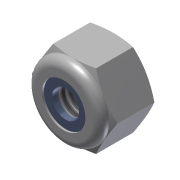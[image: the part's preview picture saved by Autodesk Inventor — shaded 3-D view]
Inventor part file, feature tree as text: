
AUTODESK INVENTOR PART (.ipt)
format: ipt  version: 2013 (Build 170138000, 138)  size: 169,472 bytes
history: native  units: in
note: dims shown in document units (in); Inventor stores cm internally (conversion verified against a paired STEP export)
features: sketch x5, extrude x2, revolve x2, projected_geometry x2, hole x1
ambient origin geometry x8: Origin, YZ Plane, XZ Plane, XY Plane, X Axis, Y Axis, Z Axis, Center Point
bodies: Solid1 (feature_tree)
feature tree (12):
  extrude  "Extrusion1"  Depth=0.195in TaperAngle=0.0deg
  revolve  "Revolution1"  [1 undecoded]
  revolve  "Revolution2"  Angle=90.0deg
  hole  "Hole1"  [1 undecoded]
  extrude  "Extrusion2"  Depth=0.027in
  sketch  "Sketch1"  dims[d0=0.3438in d1=0.195in d2=0.0in]
  sketch  "Sketch2"  dims[d5=0.039in d6=0.039in]
  sketch  "Sketch3"  dims[d7=0.133in d8=90.0deg]
  sketch  "Sketch4"  dims[d9=0.027in d10=0.012in]
  sketch  "Sketch5"  dims[d11=0.012in d12=0.027in d13=90.0deg d14=0.13in d15=0.75in d16=0.201in d17=0.009in d18=0.5635in d19=1.0in d20=0.8108in d21=0.125in d24=0.027in d25=0.0in]
  projected_geometry  "Project Cut Edges1"
  projected_geometry  "Project Cut Edges2"
note: 2 required parameter values undecoded (feature->parameter linkage not recoverable at this tier; creation-order binding heuristic only, values carry confidence <= 0.55)